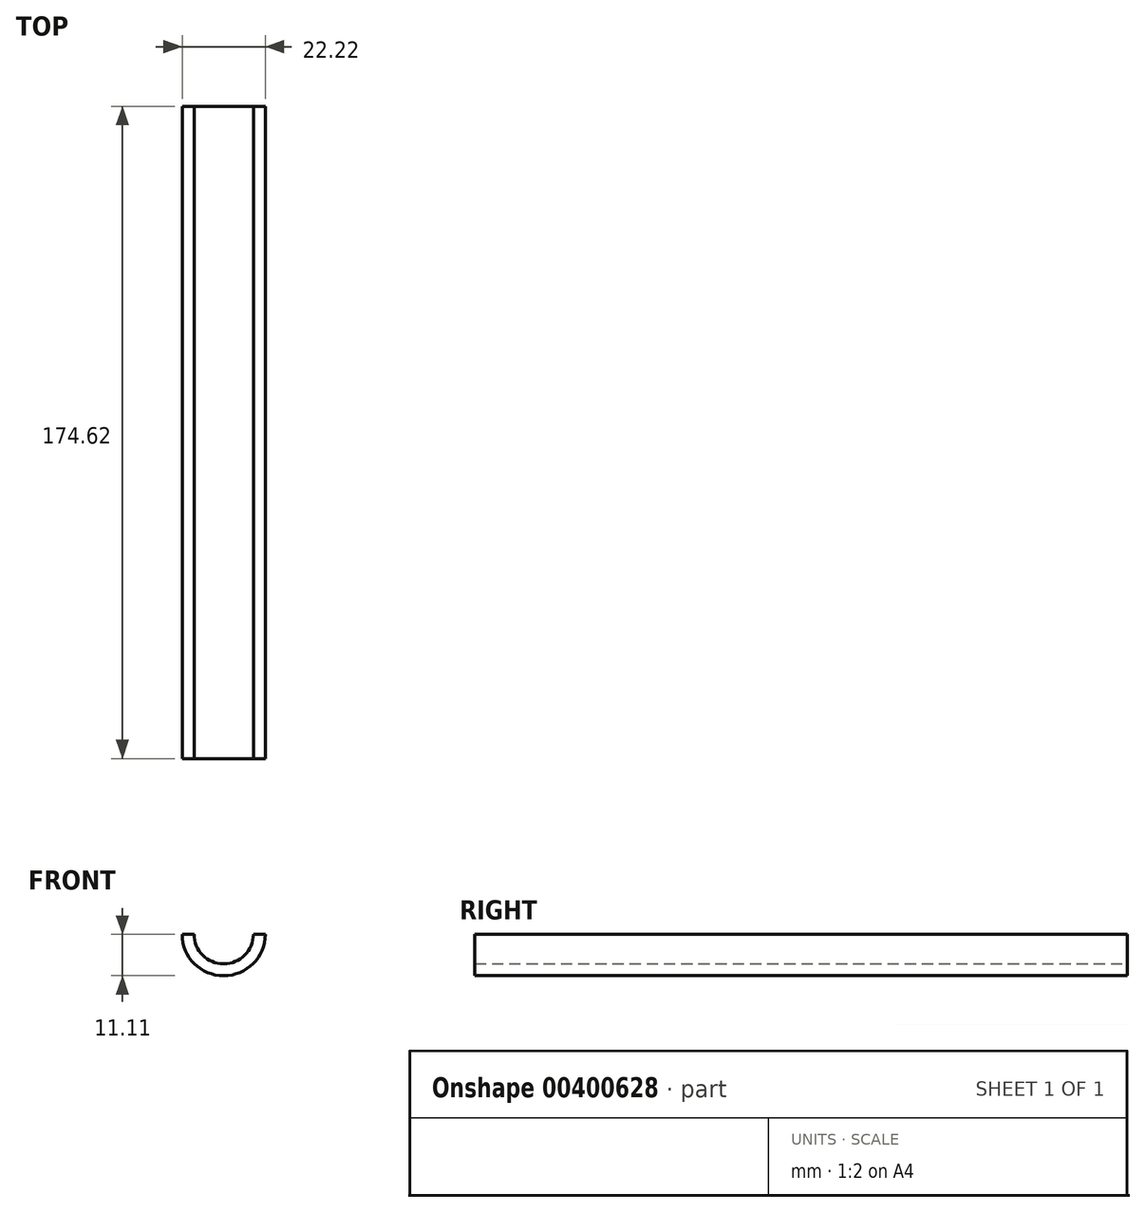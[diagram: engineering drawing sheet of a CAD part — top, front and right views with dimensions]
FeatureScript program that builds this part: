
annotation { "Feature Type Name" : "Feature", "Feature Type Description" : "" }
export const myFeature = defineFeature(function(context is Context, id is Id, definition is map)
    precondition{}
    {
        {
            var Q0;
            Q0=qCreatedBy(makeId("Front.planeOp"),FACE);
            var sketch = newSketch(context, id + "F0", { "sketchPlane" : qUnion([Q0])});
            skCircle(sketch, "E0", {"center": v(0, 0) * mm, "radius": 11.11 * mm});
            skSolve(sketch);
        }
        {
            var Q0;
            Q0 = qSketchRegion(id + "F0", true);
            extrude(context, id + "F1", {"entities" : qUnion([Q0]), "depth" : 174.62 * mm, "symmetric" : true});
        }
        {
            var Q0;
            Q0=qCreatedBy(makeId("Front.planeOp"),FACE);
            var sketch = newSketch(context, id + "F2", { "sketchPlane" : qUnion([Q0])});
            skCircle(sketch, "E1", {"center": v(0, 0) * mm, "radius": 7.94 * mm});
            skSolve(sketch);
        }
        {
            var Q0;
            Q0 = qSketchRegion(id + "F2", true);
            extrude(context, id + "F3", {"entities" : qUnion([Q0]), "operationType" : NewBodyOperationType.REMOVE, "depth" : 254 * mm, "symmetric" : true});
        }
        {
            var Q0;
            Q0=qCreatedBy(makeId("Front.planeOp"),FACE);
            var sketch = newSketch(context, id + "F4", { "sketchPlane" : qUnion([Q0])});
            skLineSegment(sketch, "E2.bottom", {"start": v(-21, 0) * mm, "end": v(20.75, 0) * mm});
            skLineSegment(sketch, "E2.top", {"start": v(-21, 12.75) * mm, "end": v(20.75, 12.75) * mm});
            skLineSegment(sketch, "E2.left", {"start": v(-21, 0) * mm, "end": v(-21, 12.75) * mm});
            skLineSegment(sketch, "E2.right", {"start": v(20.75, 0) * mm, "end": v(20.75, 12.75) * mm});
            skSolve(sketch);
        }
        {
            var Q0;
            Q0 = qSketchRegion(id + "F4", true);
            extrude(context, id + "F5", {"entities" : qUnion([Q0]), "operationType" : NewBodyOperationType.REMOVE, "oppositeDirection" : true, "depth" : 254 * mm, "symmetric" : true});
        }
    });
